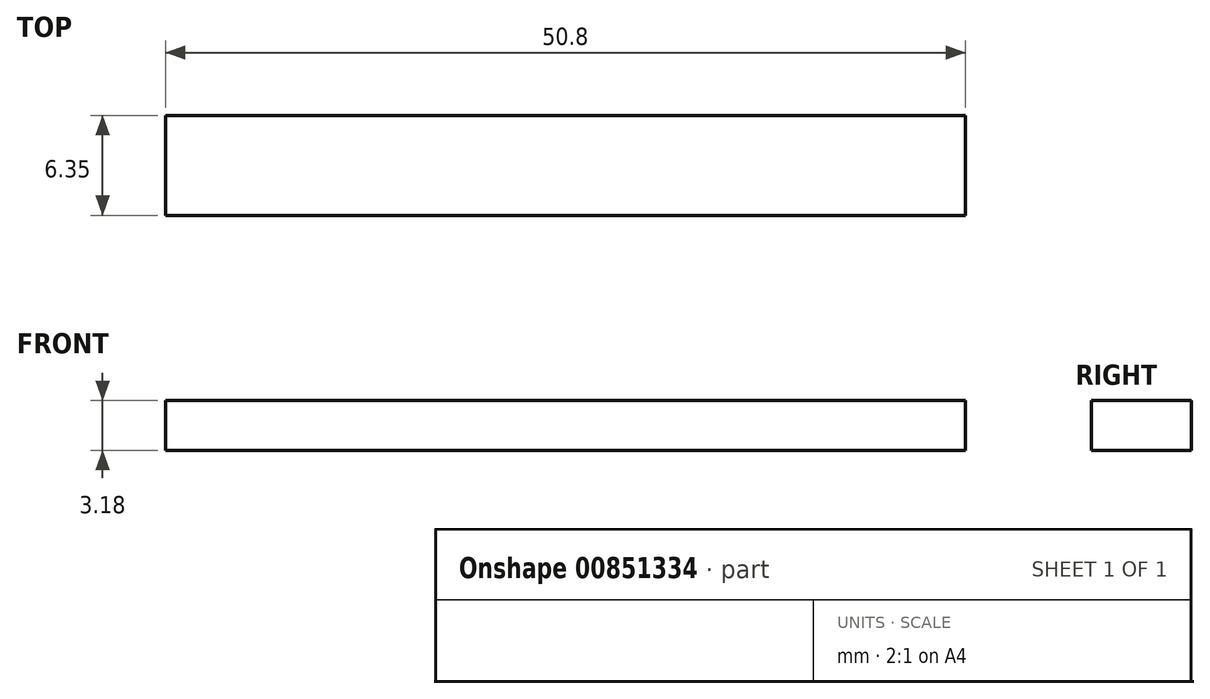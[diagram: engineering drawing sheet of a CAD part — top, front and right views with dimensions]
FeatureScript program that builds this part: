
annotation { "Feature Type Name" : "Feature", "Feature Type Description" : "" }
export const myFeature = defineFeature(function(context is Context, id is Id, definition is map)
    precondition{}
    {
        {
            var Q0;
            Q0=qCreatedBy(makeId("Front.planeOp"),FACE);
            var sketch = newSketch(context, id + "F0", { "sketchPlane" : qUnion([Q0])});
            skLineSegment(sketch, "E0.bottom", {"start": v(-8.86, 5.17) * mm, "end": v(41.94, 5.17) * mm});
            skLineSegment(sketch, "E0.top", {"start": v(-8.86, 2) * mm, "end": v(41.94, 2) * mm});
            skLineSegment(sketch, "E0.left", {"start": v(-8.86, 5.17) * mm, "end": v(-8.86, 2) * mm});
            skLineSegment(sketch, "E0.right", {"start": v(41.94, 5.17) * mm, "end": v(41.94, 2) * mm});
            skSolve(sketch);
        }
        {
            var Q0;
            Q0 = qSketchRegion(id + "F0", true);
            extrude(context, id + "F1", {"entities" : qUnion([Q0]), "depth" : 6.35 * mm, "offsetDistance" : 25.4 * mm});
        }
    });
